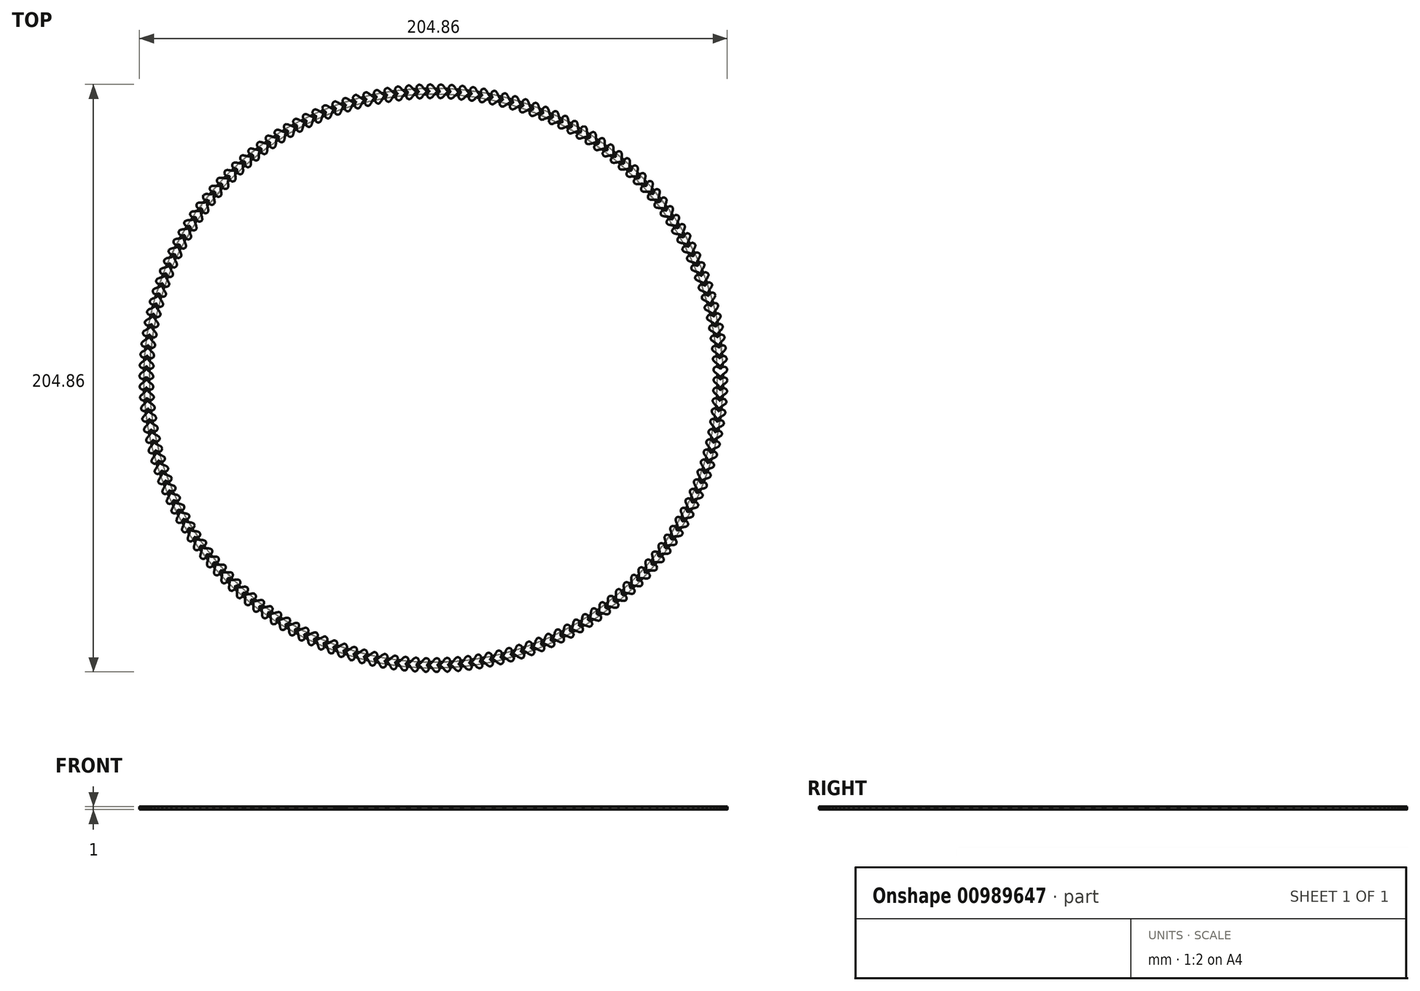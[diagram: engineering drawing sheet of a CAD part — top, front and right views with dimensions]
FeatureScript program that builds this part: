
annotation { "Feature Type Name" : "Feature", "Feature Type Description" : "" }
export const myFeature = defineFeature(function(context is Context, id is Id, definition is map)
    precondition{}
    {
        {
            var Q0;
            Q0=qCreatedBy(makeId("Top.planeOp"),FACE);
            var sketch = newSketch(context, id + "F0", { "sketchPlane" : qUnion([Q0])});
            skCircle(sketch, "E0", {"center": v(0, 0) * mm, "radius": 100 * mm, "construction": true});
            skFitSpline(sketch, "E1", {"points": [v(100, 0) * mm, v(102.38, 2.9) * mm, v(100, 3.19) * mm], "startDerivative": vector(0.12, 6.65) * mm, "endDerivative": vector(-8.42, -10.56) * mm});
            skLineSegment(sketch, "E2", {"start": v(100, 3.19) * mm, "end": v(100, 0) * mm, "construction": true});
            skFitSpline(sketch, "E3.MirrorCS", {"points": [v(100, 0) * mm, v(97.62, 2.9) * mm, v(100, 3.19) * mm], "startDerivative": vector(-0.12, 6.65) * mm, "endDerivative": vector(8.42, -10.56) * mm});
            skCircle(sketch, "E4.0", {"center": v(0, 0) * mm, "radius": 101 * mm});
            skCircle(sketch, "E5.0", {"center": v(0, 0) * mm, "radius": 99 * mm});
            skSolve(sketch);
        }
        {
            var Q0;
            {var subQ1=sQuery(id+"F0.wireOp",EDGE,"E1");Q0=makeQuery(id+"F0.imprint","IMPRINT",FACE,{"disambiguationData":[TD([[makeQuery(id+"F0.imprint","IMPRINT",EDGE,{"derivedFrom":subQ1}),1.0]])]});}
            var Q1;
            {var subQ0=sQuery(id+"F0.wireOp",EDGE,"E3.MirrorCS");var subQ1=sQuery(id+"F0.wireOp",EDGE,"E0");var subQ3=makeQuery(id+"F0.imprint","INTERSECT",VERTEX,{"derivedFrom":[subQ1,subQ0]});Q1=makeQuery(id+"F0.imprint","IMPRINT",FACE,{"disambiguationData":[TD([[makeQuery(id+"F0.imprint","IMPRINT",EDGE,{"disambiguationData":[TD([[subQ3,1.0]])],"derivedFrom":subQ1}),1.0]])]});}
            var Q2;
            {var subQ0=sQuery(id+"F0.wireOp",EDGE,"E4.0");var subQ1=sQuery(id+"F0.wireOp",EDGE,"E1");var subQ2=makeQuery(id+"F0.imprint","INTERSECT",VERTEX,{"disambiguationData":[OD(0.0)],"derivedFrom":[subQ1,subQ0]});Q2=makeQuery(id+"F0.imprint","IMPRINT",FACE,{"disambiguationData":[TD([[makeQuery(id+"F0.imprint","IMPRINT",EDGE,{"disambiguationData":[TD([[subQ2,-1.0]])],"derivedFrom":subQ1}),1.0]])]});}
            var Q3;
            {var subQ0=sQuery(id+"F0.wireOp",EDGE,"E5.0");var subQ1=sQuery(id+"F0.wireOp",EDGE,"E3.MirrorCS");var subQ2=makeQuery(id+"F0.imprint","INTERSECT",VERTEX,{"disambiguationData":[OD(0.0)],"derivedFrom":[subQ1,subQ0]});Q3=makeQuery(id+"F0.imprint","IMPRINT",FACE,{"disambiguationData":[TD([[makeQuery(id+"F0.imprint","IMPRINT",EDGE,{"disambiguationData":[TD([[subQ2,-1.0]])],"derivedFrom":subQ1}),-1.0]])]});}
            extrude(context, id + "F1", {"entities" : qUnion([Q0, Q1, Q2, Q3]), "depth" : 1 * mm, "offsetDistance" : 25 * mm});
        }
        {
            var Q0;
            Q0=qCreatedBy(makeId("Front.planeOp"),FACE);
            var sketch = newSketch(context, id + "F2", { "sketchPlane" : qUnion([Q0])});
            skLineSegment(sketch, "E6", {"start": v(0, 24.91) * mm, "end": v(0, -16.52) * mm, "construction": true});
            skSolve(sketch);
        }
        {
            var Q0;
            Q0=makeQuery(id+"F1.opExtrude","SWEPT_BODY",BODY,{"disambiguationData":[OSD([sQuery(id+"F0.wireOp",EDGE,"E1"),sQuery(id+"F0.wireOp",EDGE,"E3.MirrorCS")])]});
            var Q1;
            Q1=sQuery(id+"F2.wireOp",EDGE,"E6");
            circularPattern(context, id + "F3", {"entities" : qUnion([Q0]), "axis" : qUnion([Q1]), "angle" : 360 * degree, "instanceCount" : 170, "equalSpace" : true});
        }
        {
            var Q0;
            {var subQ0=sQuery(id+"F0.wireOp",EDGE,"E3.MirrorCS");var subQ1=sQuery(id+"F0.wireOp",EDGE,"E1");var subQ2=makeQuery(id+"F0.imprint","INTERSECT",VERTEX,{"disambiguationData":[OD(0.0)],"derivedFrom":[subQ1,subQ0]});Q0=makeQuery(id+"F0.imprint","IMPRINT",FACE,{"disambiguationData":[TD([[makeQuery(id+"F0.imprint","IMPRINT",EDGE,{"disambiguationData":[TD([[subQ2,-1.0]])],"derivedFrom":subQ1}),-1.0]])]});}
            extrude(context, id + "F4", {"entities" : qUnion([Q0]), "depth" : 0.5 * mm, "offsetDistance" : 25 * mm});
        }
    });
